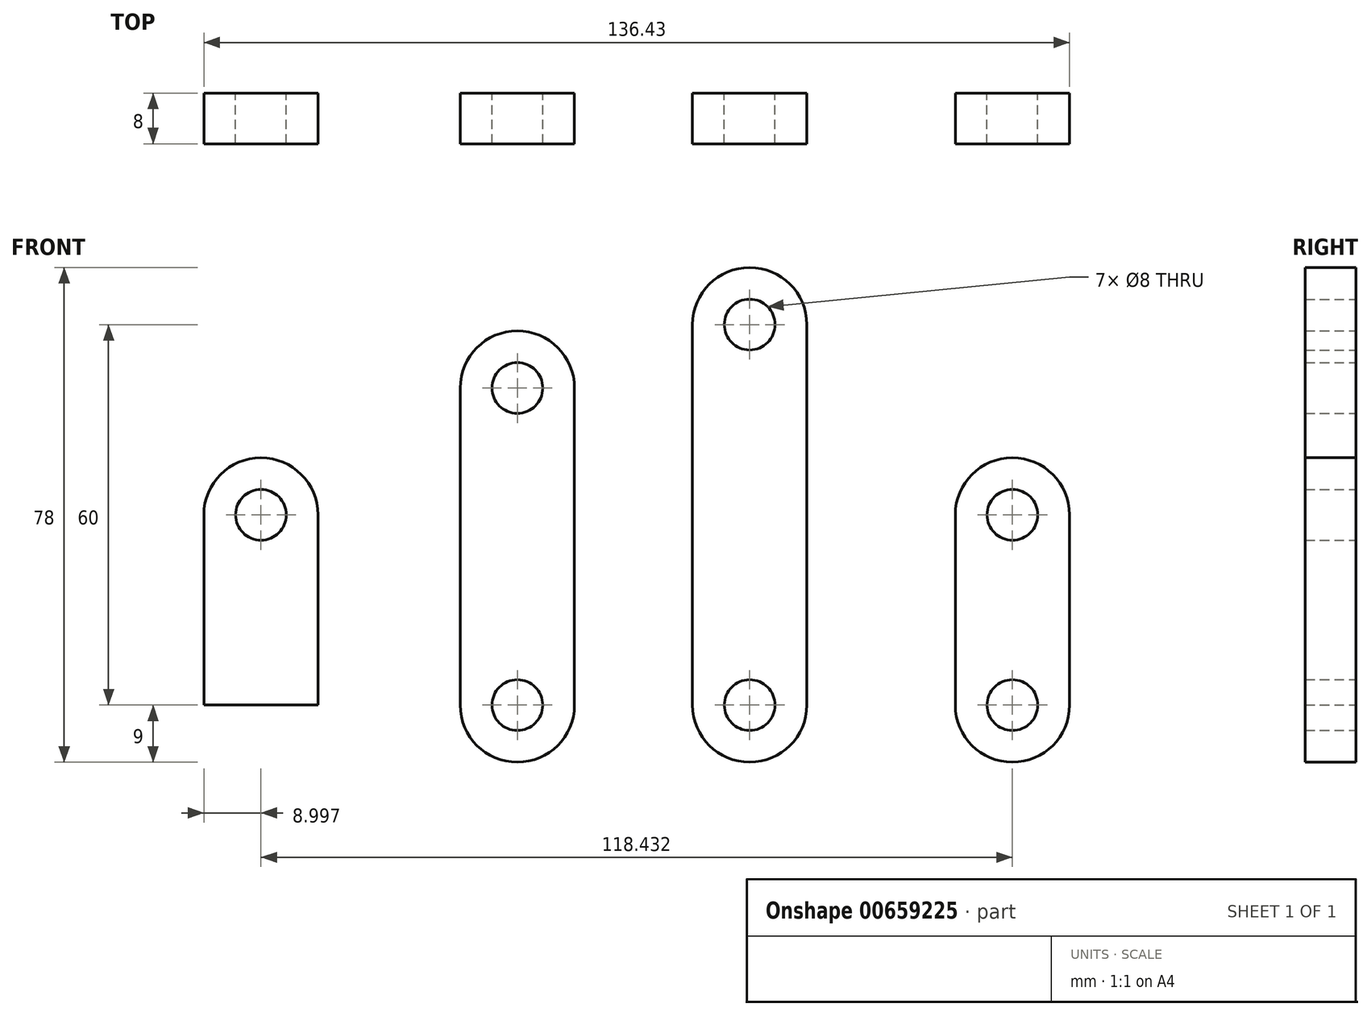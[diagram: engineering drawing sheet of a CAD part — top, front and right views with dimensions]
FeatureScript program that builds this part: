
annotation { "Feature Type Name" : "Feature", "Feature Type Description" : "" }
export const myFeature = defineFeature(function(context is Context, id is Id, definition is map)
    precondition{}
    {
        {
            assignVariable(context, id + "F0", {"name" : "thick", "anyValue" : 8});
        }
        {
            var Q0;
            Q0=qCreatedBy(makeId("Front.planeOp"),FACE);
            var sketch = newSketch(context, id + "F1", { "sketchPlane" : qUnion([Q0])});
            skArc(sketch, "E0", {"start": v(-9, 0) * mm, "mid": v(0, -9) * mm, "end": v(9, 0) * mm});
            skArc(sketch, "E1", {"start": v(9, 60) * mm, "mid": v(0, 69) * mm, "end": v(-9, 60) * mm});
            skLineSegment(sketch, "E2", {"start": v(-9, 60) * mm, "end": v(-9, 0) * mm});
            skLineSegment(sketch, "E3", {"start": v(9, 60) * mm, "end": v(9, 0) * mm});
            skCircle(sketch, "E4", {"center": v(0, 60) * mm, "radius": 4 * mm});
            skCircle(sketch, "E5", {"center": v(0, 0) * mm, "radius": 4 * mm});
            skSolve(sketch);
        }
        {
            var Q0;
            Q0=makeQuery(id+"F1.imprint","IMPRINT",FACE,{"disambiguationData":[TD([[makeQuery(id+"F1.imprint","IMPRINT",EDGE,{"derivedFrom":sQuery(id+"F1.wireOp",EDGE,"E0")}),1.0]])]});
            extrude(context, id + "F2", {"entities" : qUnion([Q0]), "depth" : (getVariable(context, 'thick')) * mm, "offsetDistance" : 25 * mm});
        }
        {
            var Q0;
            Q0=qCreatedBy(makeId("Front.planeOp"),FACE);
            var sketch = newSketch(context, id + "F3", { "sketchPlane" : qUnion([Q0])});
            skArc(sketch, "E6", {"start": v(-45.61, 0) * mm, "mid": v(-36.61, -9) * mm, "end": v(-27.61, 0) * mm});
            skArc(sketch, "E7", {"start": v(-27.61, 50) * mm, "mid": v(-36.61, 59) * mm, "end": v(-45.61, 50) * mm});
            skLineSegment(sketch, "E8", {"start": v(-45.61, 50) * mm, "end": v(-45.61, 0) * mm});
            skLineSegment(sketch, "E9", {"start": v(-27.61, 50) * mm, "end": v(-27.61, 0) * mm});
            skCircle(sketch, "E10", {"center": v(-36.61, 50) * mm, "radius": 4 * mm});
            skCircle(sketch, "E11", {"center": v(-36.61, 0) * mm, "radius": 4 * mm});
            skSolve(sketch);
        }
        {
            var Q0;
            Q0=makeQuery(id+"F3.imprint","IMPRINT",FACE,{"disambiguationData":[TD([[makeQuery(id+"F3.imprint","IMPRINT",EDGE,{"derivedFrom":sQuery(id+"F3.wireOp",EDGE,"E6")}),1.0]])]});
            extrude(context, id + "F4", {"entities" : qUnion([Q0]), "depth" : (getVariable(context, 'thick')) * mm, "offsetDistance" : 25 * mm});
        }
        {
            var Q0;
            Q0=qCreatedBy(makeId("Front.planeOp"),FACE);
            var sketch = newSketch(context, id + "F5", { "sketchPlane" : qUnion([Q0])});
            skArc(sketch, "E12", {"start": v(32.4, 0) * mm, "mid": v(41.4, -9) * mm, "end": v(50.4, 0) * mm});
            skArc(sketch, "E13", {"start": v(50.4, 30) * mm, "mid": v(41.4, 39) * mm, "end": v(32.4, 30) * mm});
            skLineSegment(sketch, "E14", {"start": v(32.4, 30) * mm, "end": v(32.4, 0) * mm});
            skLineSegment(sketch, "E15", {"start": v(50.4, 30) * mm, "end": v(50.4, 0) * mm});
            skCircle(sketch, "E16", {"center": v(41.4, 30) * mm, "radius": 4 * mm});
            skCircle(sketch, "E17", {"center": v(41.4, 0) * mm, "radius": 4 * mm});
            skSolve(sketch);
        }
        {
            var Q0;
            Q0=makeQuery(id+"F5.imprint","IMPRINT",FACE,{"disambiguationData":[TD([[makeQuery(id+"F5.imprint","IMPRINT",EDGE,{"derivedFrom":sQuery(id+"F5.wireOp",EDGE,"E12")}),1.0]])]});
            extrude(context, id + "F6", {"entities" : qUnion([Q0]), "depth" : (getVariable(context, 'thick')) * mm, "offsetDistance" : 25 * mm});
        }
        {
            var Q0;
            Q0=qCreatedBy(makeId("Front.planeOp"),FACE);
            var sketch = newSketch(context, id + "F7", { "sketchPlane" : qUnion([Q0])});
            skArc(sketch, "E18", {"start": v(-68.02, 30) * mm, "mid": v(-77.02, 39) * mm, "end": v(-86.02, 30) * mm});
            skLineSegment(sketch, "E19", {"start": v(-86.02, 30) * mm, "end": v(-86.02, 0) * mm});
            skLineSegment(sketch, "E20", {"start": v(-68.02, 30) * mm, "end": v(-68.02, 0) * mm});
            skLineSegment(sketch, "E21", {"start": v(-68.02, 0) * mm, "end": v(-86.02, 0) * mm});
            skCircle(sketch, "E22", {"center": v(-77.02, 30) * mm, "radius": 4 * mm});
            skSolve(sketch);
        }
        {
            var Q0;
            Q0=makeQuery(id+"F7.imprint","IMPRINT",FACE,{"disambiguationData":[TD([[makeQuery(id+"F7.imprint","IMPRINT",EDGE,{"derivedFrom":sQuery(id+"F7.wireOp",EDGE,"E18")}),1.0]])]});
            extrude(context, id + "F8", {"entities" : qUnion([Q0]), "depth" : (getVariable(context, 'thick')) * mm, "offsetDistance" : 25 * mm});
        }
    });
